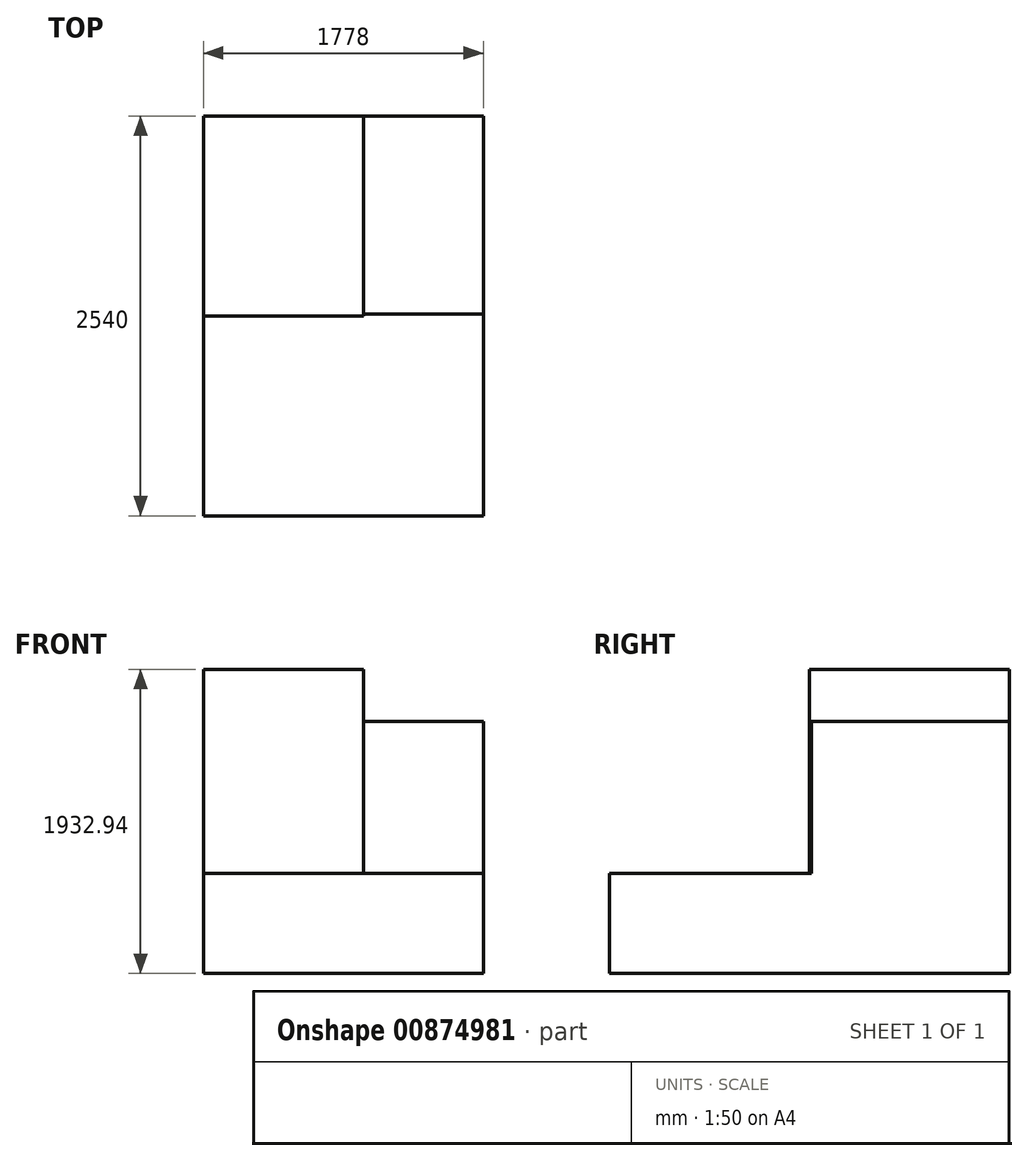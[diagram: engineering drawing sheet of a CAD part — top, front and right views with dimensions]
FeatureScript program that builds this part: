
annotation { "Feature Type Name" : "Feature", "Feature Type Description" : "" }
export const myFeature = defineFeature(function(context is Context, id is Id, definition is map)
    precondition{}
    {
        {
            var Q0;
            Q0=qCreatedBy(makeId("Top.planeOp"),FACE);
            var sketch = newSketch(context, id + "F0", { "sketchPlane" : qUnion([Q0])});
            skLineSegment(sketch, "E0.bottom", {"start": v(0, 0) * mm, "end": v(-1778, 0) * mm});
            skLineSegment(sketch, "E0.top", {"start": v(0, -2540) * mm, "end": v(-1778, -2540) * mm});
            skLineSegment(sketch, "E0.left", {"start": v(0, 0) * mm, "end": v(0, -2540) * mm});
            skLineSegment(sketch, "E0.right", {"start": v(-1778, 0) * mm, "end": v(-1778, -2540) * mm});
            skSolve(sketch);
        }
        {
            var Q0;
            Q0=makeQuery(id+"F0.imprint","IMPRINT",FACE,{"disambiguationData":[TD([[makeQuery(id+"F0.imprint","IMPRINT",EDGE,{"derivedFrom":sQuery(id+"F0.wireOp",EDGE,"E0.bottom")}),1.0]])]});
            extrude(context, id + "F1", {"entities" : qUnion([Q0]), "depth" : 635 * mm, "offsetDistance" : 25.4 * mm});
        }
        {
            var Q0;
            Q0=makeQuery(id+"F1.opExtrude","CAP_FACE",FACE,{"disambiguationData":[OSD([sQuery(id+"F0.wireOp",EDGE,"E0.bottom"),sQuery(id+"F0.wireOp",EDGE,"E0.top"),sQuery(id+"F0.wireOp",EDGE,"E0.left"),sQuery(id+"F0.wireOp",EDGE,"E0.right")])],"isStart":false});
            var sketch = newSketch(context, id + "F2", { "sketchPlane" : qUnion([Q0])});
            skLineSegment(sketch, "E1.bottom", {"start": v(-1778, 0) * mm, "end": v(-762, 0) * mm});
            skLineSegment(sketch, "E1.top", {"start": v(-1778, -1270) * mm, "end": v(-762, -1270) * mm});
            skLineSegment(sketch, "E1.left", {"start": v(-1778, 0) * mm, "end": v(-1778, -1270) * mm});
            skLineSegment(sketch, "E1.right", {"start": v(-762, 0) * mm, "end": v(-762, -1270) * mm});
            skSolve(sketch);
        }
        {
            var Q0;
            Q0 = qSketchRegion(id + "F2", true);
            extrude(context, id + "F3", {"entities" : qUnion([Q0]), "operationType" : NewBodyOperationType.ADD, "depth" : 635 * mm, "offsetDistance" : 25.4 * mm});
        }
        {
            var Q0;
            Q0=makeQuery(id+"F1.opExtrude","CAP_FACE",FACE,{"disambiguationData":[OSD([sQuery(id+"F0.wireOp",EDGE,"E0.bottom"),sQuery(id+"F0.wireOp",EDGE,"E0.top"),sQuery(id+"F0.wireOp",EDGE,"E0.left"),sQuery(id+"F0.wireOp",EDGE,"E0.right")])],"isStart":false});
            var sketch = newSketch(context, id + "F4", { "sketchPlane" : qUnion([Q0])});
            skSolve(sketch);
        }
        {
            var Q0;
            Q0=makeQuery(id+"F4.imprint","IMPRINT",FACE,{"disambiguationData":[TD([[makeQuery(id+"F4.imprint","IMPRINT",EDGE,{"derivedFrom":makeQuery(id+"F1.opExtrude","CAP_EDGE",EDGE,{"disambiguationData":[OSD([sQuery(id+"F0.wireOp",EDGE,"E0.top")])],"isStart":false})}),-1.0]])]});
            var sketch = newSketch(context, id + "F5", { "sketchPlane" : qUnion([Q0])});
            skLineSegment(sketch, "E2", {"start": v(-785.33, -1257.39) * mm, "end": v(0, -1257.39) * mm});
            skSolve(sketch);
        }
        {
            var Q0;
            {var subQ5=makeQuery(id+"F4.imprint","IMPRINT",EDGE,{"derivedFrom":makeQuery(id+"F1.opExtrude","CAP_EDGE",EDGE,{"disambiguationData":[OSD([sQuery(id+"F0.wireOp",EDGE,"E0.bottom")])],"isStart":false})});Q0=makeQuery(id+"F5.imprint","IMPRINT",FACE,{"disambiguationData":[TD([[makeQuery(id+"F5.imprint","IMPRINT",EDGE,{"derivedFrom":subQ5}),1.0]])]});}
            var sketch = newSketch(context, id + "F6", { "sketchPlane" : qUnion([Q0])});
            skSolve(sketch);
        }
        {
            var Q0;
            Q0 = qSketchRegion(id + "F6", true);
            var Q1;
            {var subQ5=makeQuery(id+"F4.imprint","IMPRINT",EDGE,{"derivedFrom":makeQuery(id+"F1.opExtrude","CAP_EDGE",EDGE,{"disambiguationData":[OSD([sQuery(id+"F0.wireOp",EDGE,"E0.bottom")])],"isStart":false})});Q1=makeQuery(id+"F5.imprint","IMPRINT",FACE,{"disambiguationData":[TD([[makeQuery(id+"F5.imprint","IMPRINT",EDGE,{"derivedFrom":subQ5}),1.0]])]});}
            extrude(context, id + "F7", {"entities" : qUnion([Q0, Q1]), "operationType" : NewBodyOperationType.ADD, "depth" : 965.2 * mm, "offsetDistance" : 25.4 * mm});
        }
        {
            var Q0;
            Q0=makeQuery(id+"F3.opExtrude","CAP_FACE",FACE,{"disambiguationData":[OSD([sQuery(id+"F2.wireOp",EDGE,"E1.bottom"),sQuery(id+"F2.wireOp",EDGE,"E1.top"),sQuery(id+"F2.wireOp",EDGE,"E1.left"),sQuery(id+"F2.wireOp",EDGE,"E1.right")])],"isStart":false});
            var sketch = newSketch(context, id + "F8", { "sketchPlane" : qUnion([Q0])});
            skSolve(sketch);
        }
        {
            var Q0;
            {var subQ3=sQuery(id+"F2.wireOp",EDGE,"E1.bottom");Q0=makeQuery(id+"F8.imprint","IMPRINT",FACE,{"disambiguationData":[TD([[makeQuery(id+"F8.imprint","IMPRINT",EDGE,{"derivedFrom":makeQuery(id+"F3.opExtrude","CAP_EDGE",EDGE,{"disambiguationData":[OSD([subQ3])],"isStart":false})}),1.0]])]});}
            extrude(context, id + "F9", {"entities" : qUnion([Q0]), "operationType" : NewBodyOperationType.ADD, "depth" : 662.94 * mm, "offsetDistance" : 25.4 * mm});
        }
    });
